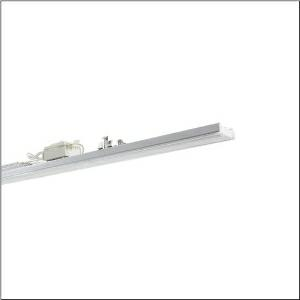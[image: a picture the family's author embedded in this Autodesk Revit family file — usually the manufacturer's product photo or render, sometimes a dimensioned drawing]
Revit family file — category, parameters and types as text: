
# Revit family: licross_11_recessed_ho_51te11dn4exs
name_source: partatom
category: Lighting Fixtures
units: mm (PartAtom-declared; Revit-internal decimal feet)

## family parameters
Cut with Voids When Loaded = No
Host = Face
Light Source = No
Part Type = Normal
Room Calculation Point = No
Round Connector Dimension = Use Diameter
Shared = No

## types (1)
- --- (1 x LED, 14000 lm, 76.8 W, 4000K)
    Apparent Load = 77 VA
    CIE Flux Codes = 87 95 99 100 100
    Color Rendering = 80
    Color Temperature = 4000K
    Default Elevation = 1800 mm
    Description = Licross 11 Recessed HO, luminaire insert, of sheet steel, galvanised, coil coated, white, length: 1.500mm, width: 66mm, height: 67mm, LED rated luminous flux: 14.000lm, light colour: 840, SDCM (Standard Deviation of Colour Matching)MacAdam ≤ 2 SDCM (initial), control gear: DALI 2, with plug, 5-pole, with phase selection, mains connection: 220..240V, AC, 50/60Hz, rated input power: 77W, internal wiring halogen-free, primary light control with lens, of plastic, primary optical cover: cover, of PMMA, light emission: direct distribution, primary light characteristic: symmetric, protection rating (complete): IP54, insulation class (complete): insulation class I (protective earthing), certification: CE, ENEC, VDE, UKCA, protection symbol: D if used in an environment with non-conductive dust loads with corresponding accessories, impact resistance: IK06, permissible ambient temperature for indoor applications: -25..+30°C, corresponds to IFS (International Featured Standards) requirements for safety and quality in the food industry, reducing of maximum allowable ambient temperature of 5°C with ceiling mounting, LABS conformity tested according to VDMA 24364:2018-05, The light source and the operating device comply with the requirements of the Ecodesign Regulation (EU) 2019/2020 and are replaceable in accordance with this regulation, packaging unit: 1 piece
    Height = 58 mm
    Lamp = 1 x LED
    Lamp Light Flux = 14000 lm
    Lamp Power = 76.8 W
    Lamp count = 1
    Length = 1500 mm
    Luminous efficacy = 182 lm/W
    Manufacturer = Siteco
    ModVariant = No
    Model = 51TE11DN4EXS
    Mounting Place = Ceiling
    Mounting Type = Pendant
    Number of Poles = 1
    OnlyDefault = Yes
    Power Factor = 1
    Product Name = Licross 11 Recessed HO
    Product group = luminaire insert | ceiling pendant
    ProductGroupID = 901
    Protection Class = Protection class I
    Protection Degree = IP 54
    RLX_Detail_Level = 1
    RLX_Emergency_Light_Flux = 0 lm
    RLX_Emergency_Type = 0
    RLX_Emergency_Type_DB = No
    RlxData = <blob elided: 24885 chars, md5=ff501483>
    Socket = socket
    Standby Power = 0 W
    System Light Flux = 14000 lm
    System Power = 77 W
    Type Comments = factory setting: luminous flux: 100 % | dim-lin: 254 | 522 mA
    Type Image = l_1296930.jpg
    URL = http://relux.com
    VarID = @adj_100445
    Voltage = 0 V
    Weight = 0.00 kg
    Width = 66 mm

## geometry (parser evidence)
native form markers: Blend x4, Sweep x11
no freeform markers — native parametric forms only
